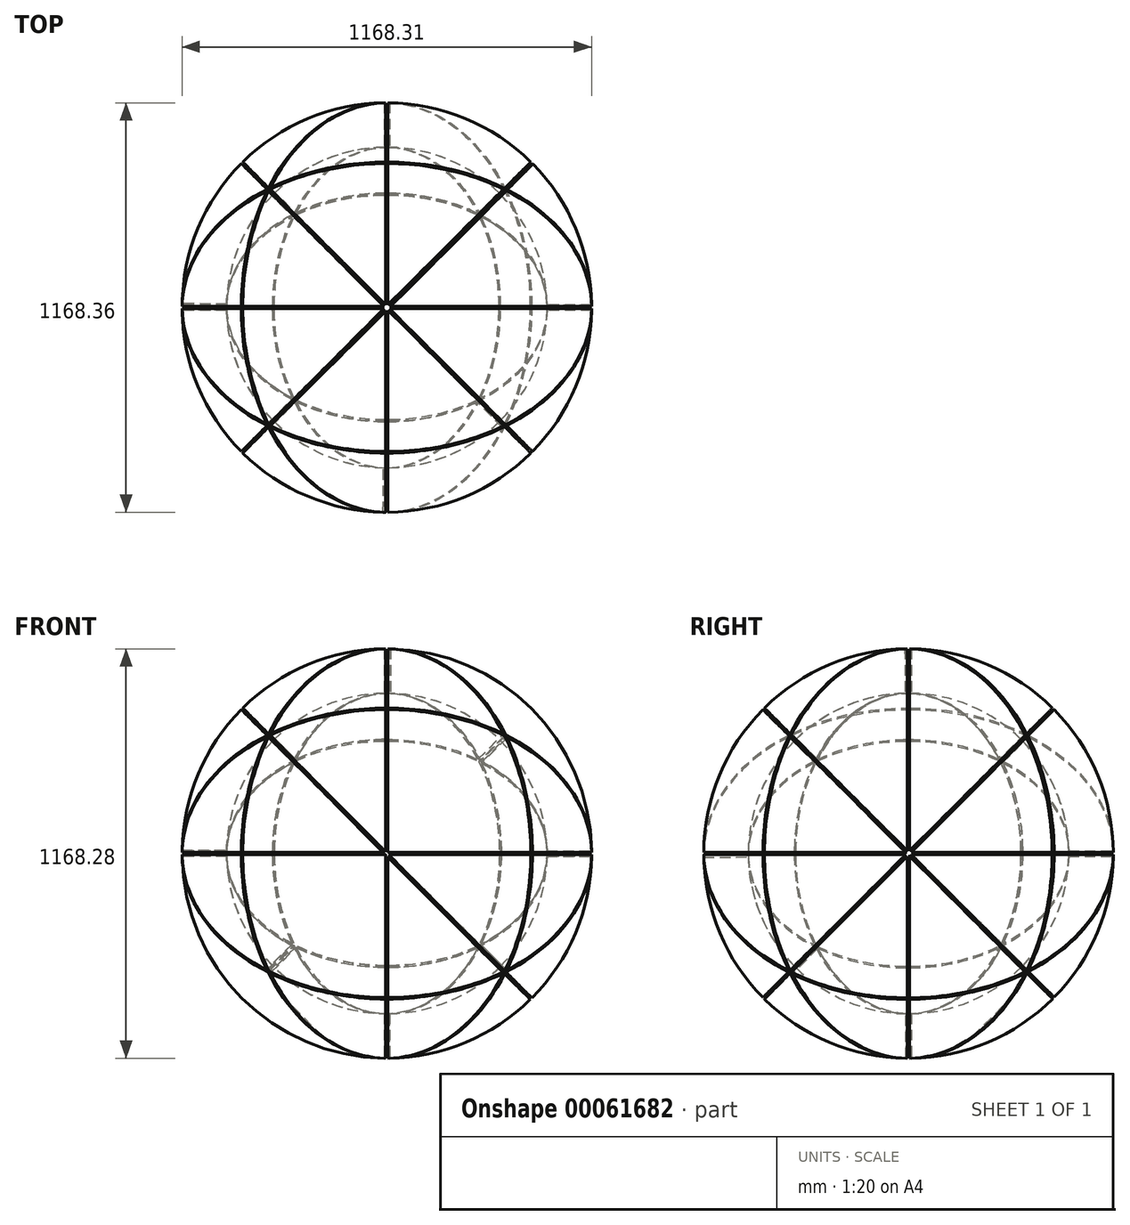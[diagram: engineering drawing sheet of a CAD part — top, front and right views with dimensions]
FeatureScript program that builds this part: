
annotation { "Feature Type Name" : "Feature", "Feature Type Description" : "" }
export const myFeature = defineFeature(function(context is Context, id is Id, definition is map)
    precondition{}
    {
        {
            var Q0;
            Q0=qCreatedBy(makeId("Front.planeOp"),FACE);
            var sketch = newSketch(context, id + "F0", { "sketchPlane" : qUnion([Q0])});
            skArc(sketch, "E0", {"start": v(0, 457.2) * mm, "mid": v(-457.2, 0) * mm, "end": v(0, -457.2) * mm});
            skArc(sketch, "E1", {"start": v(0, 584.2) * mm, "mid": v(-584.2, 0) * mm, "end": v(0, -584.2) * mm});
            skLineSegment(sketch, "E2", {"start": v(0, 457.2) * mm, "end": v(0, -457.2) * mm, "construction": true});
            skLineSegment(sketch, "E3", {"start": v(0, 584.2) * mm, "end": v(0, 457.2) * mm});
            skLineSegment(sketch, "E4", {"start": v(0, -457.2) * mm, "end": v(0, -584.2) * mm});
            skSolve(sketch);
        }
        {
            var Q0;
            Q0 = qSketchRegion(id + "F0", true);
            var Q1;
            Q1=sQuery(id+"F0.wireOp",EDGE,"E2");
            revolve(context, id + "F1", {"entities" : qUnion([Q0]), "axis" : qUnion([Q1]), "revolveType" : RevolveType.FULL});
        }
        {
            var Q0;
            Q0=qCreatedBy(makeId("Top.planeOp"),FACE);
            var sketch = newSketch(context, id + "F2", { "sketchPlane" : qUnion([Q0])});
            skLineSegment(sketch, "E5", {"start": v(0, 0) * mm, "end": v(-584.2, 0) * mm, "construction": true});
            skLineSegment(sketch, "E6.1.0", {"start": v(0, 0) * mm, "end": v(0, -584.2) * mm, "construction": true});
            skLineSegment(sketch, "E6.2.0", {"start": v(0, 0) * mm, "end": v(584.2, 0) * mm, "construction": true});
            skPoint(sketch, "E6.center", {"position": v(0, 0) * mm});
            skLineSegment(sketch, "E6.anchor2", {"start": v(0, 0) * mm, "end": v(0, 584.2) * mm, "construction": true});
            skLineSegment(sketch, "E7.0", {"start": v(3.18, 3.17) * mm, "end": v(3.18, 584.2) * mm});
            skLineSegment(sketch, "E7.1", {"start": v(3.18, -3.18) * mm, "end": v(3.18, -584.2) * mm});
            skLineSegment(sketch, "E8.0", {"start": v(-3.17, 3.18) * mm, "end": v(-3.17, 584.2) * mm});
            skLineSegment(sketch, "E8.1", {"start": v(-3.17, -3.17) * mm, "end": v(-3.18, -584.2) * mm});
            skLineSegment(sketch, "E9.0", {"start": v(3.18, -3.18) * mm, "end": v(584.2, -3.18) * mm});
            skLineSegment(sketch, "E9.1", {"start": v(-3.17, -3.17) * mm, "end": v(-584.2, -3.18) * mm});
            skLineSegment(sketch, "E10.0", {"start": v(3.18, 3.17) * mm, "end": v(584.2, 3.17) * mm});
            skLineSegment(sketch, "E10.1", {"start": v(-3.17, 3.18) * mm, "end": v(-584.2, 3.17) * mm});
            skLineSegment(sketch, "E11", {"start": v(584.2, -3.18) * mm, "end": v(584.2, 3.17) * mm});
            skLineSegment(sketch, "E12", {"start": v(3.18, 584.2) * mm, "end": v(-3.17, 584.2) * mm});
            skLineSegment(sketch, "E13", {"start": v(-584.2, -3.18) * mm, "end": v(-584.2, 3.17) * mm});
            skLineSegment(sketch, "E14", {"start": v(-3.18, -584.2) * mm, "end": v(3.18, -584.2) * mm});
            skSolve(sketch);
        }
        {
            var Q0;
            Q0 = qSketchRegion(id + "F2", true);
            extrude(context, id + "F3", {"entities" : qUnion([Q0]), "operationType" : NewBodyOperationType.REMOVE, "endBound" : BoundingType.THROUGH_ALL, "oppositeDirection" : true, "depth" : 25.4 * mm, "hasSecondDirection" : true, "secondDirectionBound" : SecondDirectionBoundingType.THROUGH_ALL, "secondDirectionOppositeDirection" : false, "secondDirectionDepth" : 25.4 * mm});
        }
        {
            var Q0;
            Q0=qCreatedBy(makeId("Right.planeOp"),FACE);
            var sketch = newSketch(context, id + "F4", { "sketchPlane" : qUnion([Q0])});
            skLineSegment(sketch, "E15", {"start": v(584.2, 0) * mm, "end": v(-584.2, 0) * mm, "construction": true});
            skLineSegment(sketch, "E16.0", {"start": v(584.2, 3175) * mm, "end": v(-584.2, 3175) * mm});
            skLineSegment(sketch, "E17.0", {"start": v(584.2, 3.17) * mm, "end": v(-584.2, 3.17) * mm});
            skLineSegment(sketch, "E18.0", {"start": v(584.2, -3.17) * mm, "end": v(-584.2, -3.18) * mm});
            skLineSegment(sketch, "E19", {"start": v(584.2, -3.17) * mm, "end": v(584.2, 3.17) * mm});
            skLineSegment(sketch, "E20", {"start": v(-584.2, 3.17) * mm, "end": v(-584.2, -3.18) * mm});
            skSolve(sketch);
        }
        {
            var Q0;
            Q0 = qSketchRegion(id + "F4", true);
            extrude(context, id + "F5", {"entities" : qUnion([Q0]), "operationType" : NewBodyOperationType.REMOVE, "endBound" : BoundingType.THROUGH_ALL, "oppositeDirection" : true, "depth" : 25.4 * mm, "hasSecondDirection" : true, "secondDirectionBound" : SecondDirectionBoundingType.THROUGH_ALL, "secondDirectionOppositeDirection" : false, "secondDirectionDepth" : 25.4 * mm});
        }
        {
            var Q0;
            Q0=makeQuery(id+"F3.boolean.opBoolean","INTERSECT",VERTEX,{"disambiguationData":[OD(1.0)],"derivedFrom":[makeQuery(id+"F1.opRevolve","SWEPT_FACE",FACE,{"disambiguationData":[OSD([sQuery(id+"F0.wireOp",EDGE,"E0")])]}),makeQuery(id+"F3.opExtrude","SWEPT_FACE",FACE,{"disambiguationData":[OSD([sQuery(id+"F2.wireOp",EDGE,"E7.0")])]}),makeQuery(id+"F3.opExtrude","SWEPT_FACE",FACE,{"disambiguationData":[OSD([sQuery(id+"F2.wireOp",EDGE,"E10.0")])]})]});
            var Q1;
            {var subQ0=makeQuery(id+"F3.opExtrude","SWEPT_FACE",FACE,{"disambiguationData":[OSD([sQuery(id+"F2.wireOp",EDGE,"E7.0")])]});Q1=makeQuery(id+"F5.boolean.opBoolean","INTERSECT",VERTEX,{"derivedFrom":[makeQuery(id+"F3.boolean.opBoolean","COPY",FACE,{"derivedFrom":subQ0}),makeQuery(id+"F3.boolean.opBoolean","SPLIT",FACE,{"disambiguationData":[TD([subQ0])],"derivedFrom":makeQuery(id+"F1.opRevolve","SWEPT_FACE",FACE,{"disambiguationData":[OSD([sQuery(id+"F0.wireOp",EDGE,"E0")])]})}),makeQuery(id+"F5.opExtrude","SWEPT_FACE",FACE,{"disambiguationData":[OSD([sQuery(id+"F4.wireOp",EDGE,"E17.0")])]})]});}
            var Q2;
            {var subQ0=makeQuery(id+"F3.opExtrude","SWEPT_FACE",FACE,{"disambiguationData":[OSD([sQuery(id+"F2.wireOp",EDGE,"E10.0")])]});Q2=makeQuery(id+"F5.boolean.opBoolean","INTERSECT",VERTEX,{"derivedFrom":[makeQuery(id+"F3.boolean.opBoolean","COPY",FACE,{"derivedFrom":subQ0}),makeQuery(id+"F3.boolean.opBoolean","SPLIT",FACE,{"disambiguationData":[TD([makeQuery(id+"F3.opExtrude","SWEPT_FACE",FACE,{"disambiguationData":[OSD([sQuery(id+"F2.wireOp",EDGE,"E7.0")])]})])],"derivedFrom":makeQuery(id+"F1.opRevolve","SWEPT_FACE",FACE,{"disambiguationData":[OSD([sQuery(id+"F0.wireOp",EDGE,"E0")])]})}),makeQuery(id+"F5.opExtrude","SWEPT_FACE",FACE,{"disambiguationData":[OSD([sQuery(id+"F4.wireOp",EDGE,"E17.0")])]})]});}
            cPlane(context, id + "F6", {"entities" : qUnion([Q0, Q1, Q2]), "cplaneType" : CPlaneType.THREE_POINT, "offset" : 152.4 * mm, "width" : 152.4 * mm, "height" : 152.4 * mm});
        }
        {
            var Q0;
            {var subQ0=makeQuery(id+"F3.opExtrude","SWEPT_FACE",FACE,{"disambiguationData":[OSD([sQuery(id+"F2.wireOp",EDGE,"E10.1")])]});Q0=makeQuery(id+"F5.boolean.opBoolean","INTERSECT",VERTEX,{"derivedFrom":[makeQuery(id+"F3.boolean.opBoolean","COPY",FACE,{"derivedFrom":subQ0}),makeQuery(id+"F3.boolean.opBoolean","SPLIT",FACE,{"disambiguationData":[TD([makeQuery(id+"F3.opExtrude","SWEPT_FACE",FACE,{"disambiguationData":[OSD([sQuery(id+"F2.wireOp",EDGE,"E8.0")])]})])],"derivedFrom":makeQuery(id+"F1.opRevolve","SWEPT_FACE",FACE,{"disambiguationData":[OSD([sQuery(id+"F0.wireOp",EDGE,"E0")])]})}),makeQuery(id+"F5.opExtrude","SWEPT_FACE",FACE,{"disambiguationData":[OSD([sQuery(id+"F4.wireOp",EDGE,"E17.0")])]})]});}
            var Q1;
            {var subQ0=makeQuery(id+"F3.opExtrude","SWEPT_FACE",FACE,{"disambiguationData":[OSD([sQuery(id+"F2.wireOp",EDGE,"E8.0")])]});Q1=makeQuery(id+"F5.boolean.opBoolean","INTERSECT",VERTEX,{"derivedFrom":[makeQuery(id+"F3.boolean.opBoolean","COPY",FACE,{"derivedFrom":subQ0}),makeQuery(id+"F3.boolean.opBoolean","SPLIT",FACE,{"disambiguationData":[TD([subQ0])],"derivedFrom":makeQuery(id+"F1.opRevolve","SWEPT_FACE",FACE,{"disambiguationData":[OSD([sQuery(id+"F0.wireOp",EDGE,"E0")])]})}),makeQuery(id+"F5.opExtrude","SWEPT_FACE",FACE,{"disambiguationData":[OSD([sQuery(id+"F4.wireOp",EDGE,"E17.0")])]})]});}
            var Q2;
            Q2=makeQuery(id+"F3.boolean.opBoolean","INTERSECT",VERTEX,{"disambiguationData":[OD(1.0)],"derivedFrom":[makeQuery(id+"F1.opRevolve","SWEPT_FACE",FACE,{"disambiguationData":[OSD([sQuery(id+"F0.wireOp",EDGE,"E0")])]}),makeQuery(id+"F3.opExtrude","SWEPT_FACE",FACE,{"disambiguationData":[OSD([sQuery(id+"F2.wireOp",EDGE,"E8.0")])]}),makeQuery(id+"F3.opExtrude","SWEPT_FACE",FACE,{"disambiguationData":[OSD([sQuery(id+"F2.wireOp",EDGE,"E10.1")])]})]});
            cPlane(context, id + "F7", {"entities" : qUnion([Q0, Q1, Q2]), "cplaneType" : CPlaneType.THREE_POINT, "offset" : 152.4 * mm, "width" : 152.4 * mm, "height" : 152.4 * mm});
        }
        {
            var Q0;
            Q0=qCreatedBy(makeId("Top.planeOp"),FACE);
            var sketch = newSketch(context, id + "F8", { "sketchPlane" : qUnion([Q0])});
            skLineSegment(sketch, "E21", {"start": v(861.45, 0) * mm, "end": v(0, 0) * mm});
            skLineSegment(sketch, "E22", {"start": v(0, 0) * mm, "end": v(541.6, 541.6) * mm});
            skSolve(sketch);
        }
        {
            var Q0;
            Q0=qCreatedBy(makeId("Front.planeOp"),FACE);
            var sketch = newSketch(context, id + "F9", { "sketchPlane" : qUnion([Q0])});
            skLineSegment(sketch, "E23", {"start": v(0, 0) * mm, "end": v(0, 315.5) * mm});
            skSolve(sketch);
        }
        {
            var Q0;
            Q0=sQuery(id+"F9.wireOp",VERTEX,"E23.start");
            var Q1;
            Q1=sQuery(id+"F9.wireOp",VERTEX,"E23.end");
            var Q2;
            Q2=sQuery(id+"F8.wireOp",VERTEX,"E22.end");
            cPlane(context, id + "F10", {"entities" : qUnion([Q0, Q1, Q2]), "cplaneType" : CPlaneType.THREE_POINT, "offset" : 152.4 * mm, "width" : 152.4 * mm, "height" : 152.4 * mm});
        }
        {
            var Q0;
            {var subQ0=makeQuery(id+"F3.opExtrude","SWEPT_FACE",FACE,{"disambiguationData":[OSD([sQuery(id+"F2.wireOp",EDGE,"E8.1")])]});Q0=makeQuery(id+"F5.boolean.opBoolean","INTERSECT",VERTEX,{"derivedFrom":[makeQuery(id+"F3.boolean.opBoolean","COPY",FACE,{"derivedFrom":subQ0}),makeQuery(id+"F3.boolean.opBoolean","SPLIT",FACE,{"disambiguationData":[TD([subQ0])],"derivedFrom":makeQuery(id+"F1.opRevolve","SWEPT_FACE",FACE,{"disambiguationData":[OSD([sQuery(id+"F0.wireOp",EDGE,"E0")])]})}),makeQuery(id+"F5.opExtrude","SWEPT_FACE",FACE,{"disambiguationData":[OSD([sQuery(id+"F4.wireOp",EDGE,"E17.0")])]})]});}
            var Q1;
            {var subQ0=makeQuery(id+"F3.opExtrude","SWEPT_FACE",FACE,{"disambiguationData":[OSD([sQuery(id+"F2.wireOp",EDGE,"E9.1")])]});Q1=makeQuery(id+"F5.boolean.opBoolean","INTERSECT",VERTEX,{"derivedFrom":[makeQuery(id+"F3.boolean.opBoolean","COPY",FACE,{"derivedFrom":subQ0}),makeQuery(id+"F3.boolean.opBoolean","SPLIT",FACE,{"disambiguationData":[TD([makeQuery(id+"F3.opExtrude","SWEPT_FACE",FACE,{"disambiguationData":[OSD([sQuery(id+"F2.wireOp",EDGE,"E8.1")])]})])],"derivedFrom":makeQuery(id+"F1.opRevolve","SWEPT_FACE",FACE,{"disambiguationData":[OSD([sQuery(id+"F0.wireOp",EDGE,"E0")])]})}),makeQuery(id+"F5.opExtrude","SWEPT_FACE",FACE,{"disambiguationData":[OSD([sQuery(id+"F4.wireOp",EDGE,"E17.0")])]})]});}
            var Q2;
            Q2=makeQuery(id+"F3.boolean.opBoolean","INTERSECT",VERTEX,{"disambiguationData":[OD(1.0)],"derivedFrom":[makeQuery(id+"F1.opRevolve","SWEPT_FACE",FACE,{"disambiguationData":[OSD([sQuery(id+"F0.wireOp",EDGE,"E0")])]}),makeQuery(id+"F3.opExtrude","SWEPT_FACE",FACE,{"disambiguationData":[OSD([sQuery(id+"F2.wireOp",EDGE,"E8.1")])]}),makeQuery(id+"F3.opExtrude","SWEPT_FACE",FACE,{"disambiguationData":[OSD([sQuery(id+"F2.wireOp",EDGE,"E9.1")])]})]});
            cPlane(context, id + "F11", {"entities" : qUnion([Q0, Q1, Q2]), "cplaneType" : CPlaneType.THREE_POINT, "offset" : 152.4 * mm, "width" : 152.4 * mm, "height" : 152.4 * mm});
        }
        {
            var Q0;
            Q0=qCreatedBy(id+"F11.planeOp",FACE);
            var sketch = newSketch(context, id + "F12", { "sketchPlane" : qUnion([Q0])});
            skLineSegment(sketch, "E24", {"start": v(0, 0) * mm, "end": v(-335.2, 580.58) * mm, "construction": true});
            skLineSegment(sketch, "E25", {"start": v(0, 0) * mm, "end": v(-302.22, -523.46) * mm, "construction": true});
            skLineSegment(sketch, "E26", {"start": v(0, 0) * mm, "end": v(798.45, 0) * mm, "construction": true});
            skLineSegment(sketch, "E27.0", {"start": v(1.83, -3.18) * mm, "end": v(788.27, -3.18) * mm});
            skLineSegment(sketch, "E27.1", {"start": v(1.83, -3.17) * mm, "end": v(-299.47, -525.04) * mm});
            skLineSegment(sketch, "E28.0", {"start": v(-3.67, 0) * mm, "end": v(-304.97, -521.87) * mm});
            skLineSegment(sketch, "E28.1", {"start": v(-3.67, 0) * mm, "end": v(-337.95, 579) * mm});
            skLineSegment(sketch, "E29.0", {"start": v(1.83, 3.18) * mm, "end": v(-332.45, 582.17) * mm});
            skLineSegment(sketch, "E29.1", {"start": v(768.83, 3.18) * mm, "end": v(1.83, 3.18) * mm});
            skLineSegment(sketch, "E30", {"start": v(768.83, 3.18) * mm, "end": v(788.27, -3.18) * mm});
            skLineSegment(sketch, "E31", {"start": v(-337.95, 579) * mm, "end": v(-332.45, 582.17) * mm});
            skLineSegment(sketch, "E32", {"start": v(-299.47, -525.04) * mm, "end": v(-304.97, -521.87) * mm});
            skPoint(sketch, "E33.orphan", {"position": v(798.45, -6.5) * mm});
            skPoint(sketch, "E34.orphan", {"position": v(798.45, -3.17) * mm});
            skLineSegment(sketch, "E35", {"start": v(0, 0) * mm, "end": v(1.83, 866.25) * mm, "construction": true});
            skLineSegment(sketch, "E36.MirrorCS", {"start": v(297.24, -526.3) * mm, "end": v(302.76, -523.16) * mm});
            skLineSegment(sketch, "E37.MirrorCS", {"start": v(-768.81, 6.43) * mm, "end": v(-788.28, 0.16) * mm});
            skLineSegment(sketch, "E38.MirrorCS", {"start": v(340.4, 577.56) * mm, "end": v(334.9, 580.76) * mm});
            skLineSegment(sketch, "E39.MirrorCS", {"start": v(0, 0) * mm, "end": v(300, -524.73) * mm, "construction": true});
            skPoint(sketch, "E40.MirrorP", {"position": v(-798.45, 0.2) * mm});
            skLineSegment(sketch, "E41.MirrorCS", {"start": v(0, 0) * mm, "end": v(337.65, 579.16) * mm, "construction": true});
            skLineSegment(sketch, "E42.MirrorCS", {"start": v(0, 0) * mm, "end": v(-798.44, 3.38) * mm, "construction": true});
            skLineSegment(sketch, "E43.MirrorCS", {"start": v(-768.81, 6.43) * mm, "end": v(-1.82, 3.18) * mm});
            skPoint(sketch, "E44.MirrorP", {"position": v(-798.47, -3.12) * mm});
            skLineSegment(sketch, "E45.MirrorCS", {"start": v(3.67, -0.02) * mm, "end": v(340.4, 577.56) * mm});
            skLineSegment(sketch, "E46.MirrorCS", {"start": v(3.67, -0.02) * mm, "end": v(302.76, -523.16) * mm});
            skLineSegment(sketch, "E47.MirrorCS", {"start": v(-1.85, -3.17) * mm, "end": v(-788.28, 0.16) * mm});
            skLineSegment(sketch, "E48.MirrorCS", {"start": v(-1.85, -3.17) * mm, "end": v(297.24, -526.3) * mm});
            skLineSegment(sketch, "E49.MirrorCS", {"start": v(-1.82, 3.18) * mm, "end": v(334.9, 580.76) * mm});
            skSolve(sketch);
        }
        {
            var Q0;
            Q0 = qSketchRegion(id + "F12", true);
            extrude(context, id + "F13", {"entities" : qUnion([Q0]), "operationType" : NewBodyOperationType.REMOVE, "endBound" : BoundingType.THROUGH_ALL, "depth" : 25.4 * mm, "hasSecondDirection" : true, "secondDirectionBound" : SecondDirectionBoundingType.THROUGH_ALL, "secondDirectionOppositeDirection" : true, "secondDirectionDepth" : 25.4 * mm});
        }
        {
            var Q0;
            Q0=qCreatedBy(id+"F6.planeOp",FACE);
            var sketch = newSketch(context, id + "F14", { "sketchPlane" : qUnion([Q0])});
            skLineSegment(sketch, "E50", {"start": v(0, 0) * mm, "end": v(919.56, 0) * mm, "construction": true});
            skLineSegment(sketch, "E51", {"start": v(0, 0) * mm, "end": v(-470.76, -815.39) * mm, "construction": true});
            skLineSegment(sketch, "E52", {"start": v(-933.45, 0) * mm, "end": v(0, 0) * mm, "construction": true});
            skLineSegment(sketch, "E53", {"start": v(430.8, 746.16) * mm, "end": v(0, 0) * mm, "construction": true});
            skLineSegment(sketch, "E54.0", {"start": v(-5.5, -3.17) * mm, "end": v(-473.51, -813.8) * mm});
            skLineSegment(sketch, "E54.1", {"start": v(-933.45, -3.18) * mm, "end": v(-5.5, -3.18) * mm});
            skLineSegment(sketch, "E55.0", {"start": v(428.05, 747.75) * mm, "end": v(-1.83, 3.17) * mm});
            skLineSegment(sketch, "E55.1", {"start": v(-933.45, 3.17) * mm, "end": v(-1.83, 3.17) * mm});
            skLineSegment(sketch, "E56.0", {"start": v(5.5, 3.18) * mm, "end": v(919.56, 3.18) * mm});
            skLineSegment(sketch, "E56.1", {"start": v(433.55, 744.57) * mm, "end": v(5.5, 3.17) * mm});
            skLineSegment(sketch, "E57.0", {"start": v(1.83, -3.18) * mm, "end": v(919.56, -3.18) * mm});
            skLineSegment(sketch, "E57.1", {"start": v(-348.94, -610.72) * mm, "end": v(1.83, -3.17) * mm});
            skLineSegment(sketch, "E58", {"start": v(-473.51, -813.8) * mm, "end": v(-348.94, -610.72) * mm});
            skLineSegment(sketch, "E59", {"start": v(919.56, -3.18) * mm, "end": v(919.56, 3.18) * mm});
            skLineSegment(sketch, "E60", {"start": v(433.55, 744.57) * mm, "end": v(428.05, 747.75) * mm});
            skLineSegment(sketch, "E61", {"start": v(-933.45, -3.18) * mm, "end": v(-933.45, 3.17) * mm});
            skSolve(sketch);
        }
        {
            var Q0;
            Q0 = qSketchRegion(id + "F14", true);
            extrude(context, id + "F15", {"entities" : qUnion([Q0]), "operationType" : NewBodyOperationType.REMOVE, "endBound" : BoundingType.THROUGH_ALL, "oppositeDirection" : true, "depth" : 25.4 * mm, "hasSecondDirection" : true, "secondDirectionBound" : SecondDirectionBoundingType.THROUGH_ALL, "secondDirectionOppositeDirection" : false, "secondDirectionDepth" : 25.4 * mm});
        }
        {
            var Q0;
            Q0=qCreatedBy(id+"F7.planeOp",FACE);
            var sketch = newSketch(context, id + "F16", { "sketchPlane" : qUnion([Q0])});
            skLineSegment(sketch, "E62", {"start": v(0, 0) * mm, "end": v(288.72, -500.08) * mm, "construction": true});
            skLineSegment(sketch, "E63", {"start": v(674.63, 0) * mm, "end": v(0, 0) * mm, "construction": true});
            skLineSegment(sketch, "E64", {"start": v(0, 0) * mm, "end": v(-547.5, 948.3) * mm, "construction": true});
            skLineSegment(sketch, "E65.0", {"start": v(2.75, 1.59) * mm, "end": v(-544.75, 949.88) * mm});
            skLineSegment(sketch, "E65.1", {"start": v(2.75, 1.59) * mm, "end": v(291.47, -498.5) * mm});
            skLineSegment(sketch, "E66.0", {"start": v(-2.75, -1.59) * mm, "end": v(285.97, -501.67) * mm});
            skLineSegment(sketch, "E66.1", {"start": v(-2.75, -1.59) * mm, "end": v(-550.25, 946.7) * mm});
            skLineSegment(sketch, "E67", {"start": v(285.97, -501.67) * mm, "end": v(291.47, -498.5) * mm});
            skLineSegment(sketch, "E68", {"start": v(-550.25, 946.7) * mm, "end": v(-544.75, 949.88) * mm});
            skSolve(sketch);
        }
        {
            var Q0;
            Q0 = qSketchRegion(id + "F16", true);
            extrude(context, id + "F17", {"entities" : qUnion([Q0]), "operationType" : NewBodyOperationType.REMOVE, "endBound" : BoundingType.THROUGH_ALL, "oppositeDirection" : true, "depth" : 25.4 * mm, "hasSecondDirection" : true, "secondDirectionBound" : SecondDirectionBoundingType.THROUGH_ALL, "secondDirectionOppositeDirection" : false, "secondDirectionDepth" : 25.4 * mm});
        }
    });
